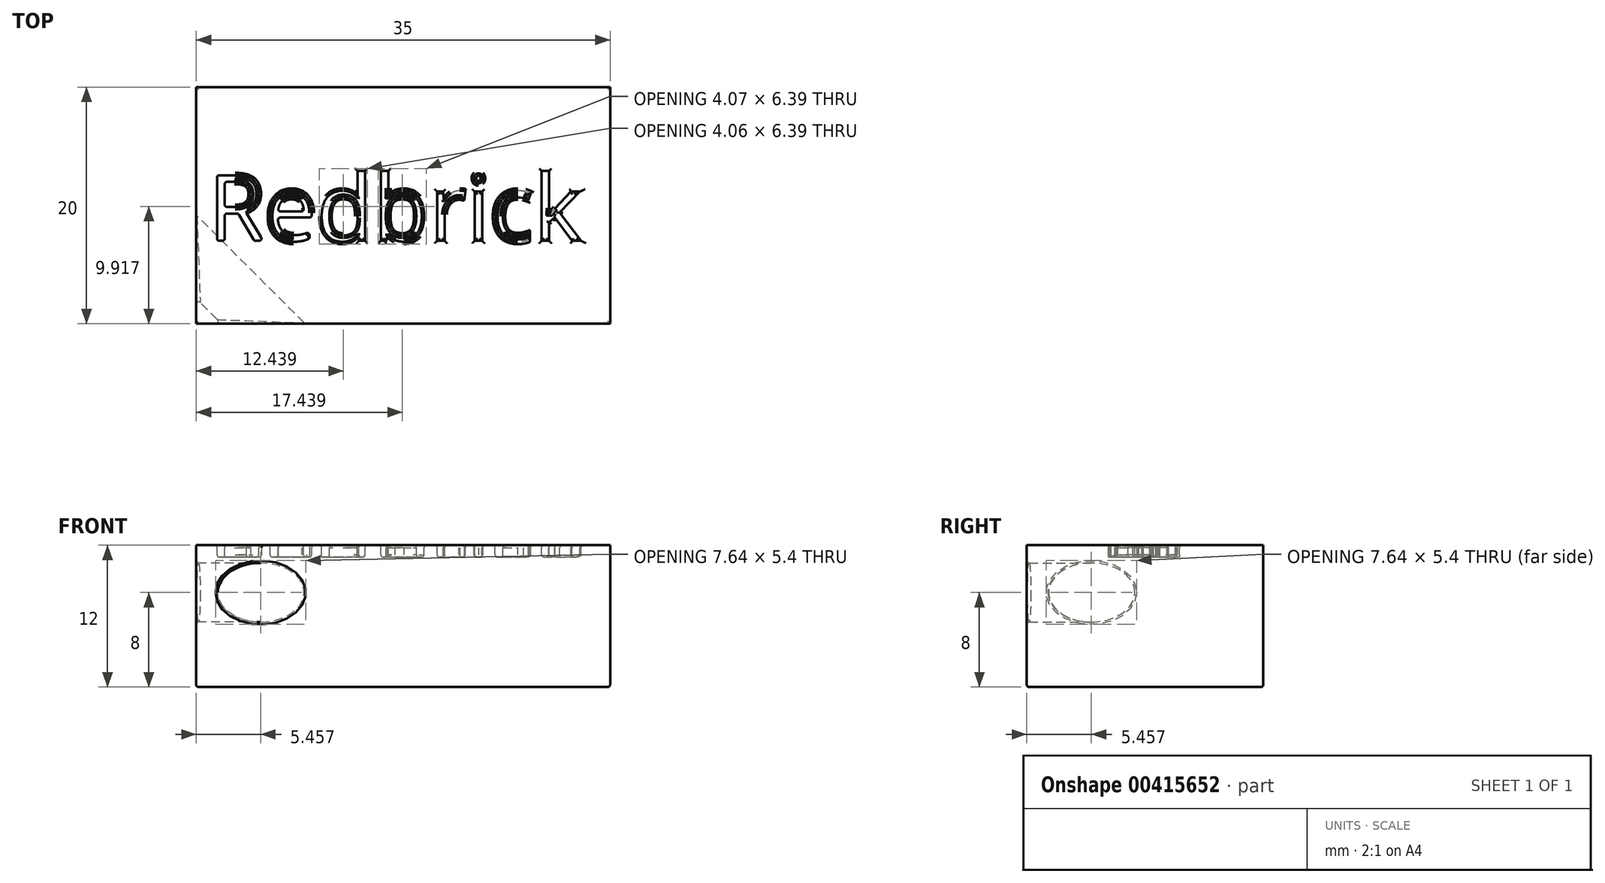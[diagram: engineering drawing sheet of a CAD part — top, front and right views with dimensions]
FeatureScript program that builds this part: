
annotation { "Feature Type Name" : "Feature", "Feature Type Description" : "" }
export const myFeature = defineFeature(function(context is Context, id is Id, definition is map)
    precondition{}
    {
        {
            var Q0;
            Q0=qCreatedBy(makeId("Top.planeOp"),FACE);
            var sketch = newSketch(context, id + "F0", { "sketchPlane" : qUnion([Q0])});
            skLineSegment(sketch, "E0.bottom", {"start": v(0, 0) * mm, "end": v(35, 0) * mm});
            skLineSegment(sketch, "E0.top", {"start": v(0, 20) * mm, "end": v(35, 20) * mm});
            skLineSegment(sketch, "E0.left", {"start": v(0, 0) * mm, "end": v(0, 20) * mm});
            skLineSegment(sketch, "E0.right", {"start": v(35, 0) * mm, "end": v(35, 20) * mm});
            skSolve(sketch);
        }
        {
            var Q0;
            Q0 = qSketchRegion(id + "F0", true);
            extrude(context, id + "F1", {"entities" : qUnion([Q0]), "depth" : 12 * mm});
        }
        {
            var Q0;
            Q0=makeQuery(id+"F1.opExtrude","SWEPT_EDGE",EDGE,{"disambiguationData":[OSD([sQuery(id+"F0.wireOp",EDGE,"E0.bottom"),sQuery(id+"F0.wireOp",EDGE,"E0.left")])]});
            cPlane(context, id + "F2", {"entities" : qUnion([Q0]), "cplaneType" : CPlaneType.LINE_ANGLE, "offset" : 25 * mm, "angle" : 45 * degree, "width" : 150 * mm, "height" : 150 * mm});
        }
        {
            var Q0;
            Q0=qCreatedBy(id+"F2.planeOp",FACE);
            var sketch = newSketch(context, id + "F3", { "sketchPlane" : qUnion([Q0])});
            skCircle(sketch, "E1", {"center": v(-4, 8) * mm, "radius": 2.5 * mm});
            skSolve(sketch);
        }
        {
            var Q0;
            Q0 = qSketchRegion(id + "F3", true);
            extrude(context, id + "F4", {"entities" : qUnion([Q0]), "operationType" : NewBodyOperationType.REMOVE, "endBound" : BoundingType.THROUGH_ALL, "oppositeDirection" : true, "depth" : 25 * mm, "hasSecondDirection" : true, "secondDirectionOppositeDirection" : false, "secondDirectionDepth" : 24.5 * mm});
        }
        {
            var Q0;
            Q0=makeQuery(id+"F1.opExtrude","CAP_FACE",FACE,{"disambiguationData":[OSD([sQuery(id+"F0.wireOp",EDGE,"E0.bottom"),sQuery(id+"F0.wireOp",EDGE,"E0.top"),sQuery(id+"F0.wireOp",EDGE,"E0.left"),sQuery(id+"F0.wireOp",EDGE,"E0.right")])],"isStart":false});
            var sketch = newSketch(context, id + "F5", { "sketchPlane" : qUnion([Q0])});
            skText(sketch, "E2", { "text": "Redbrick", "fontName": "OpenSans-Regular.ttf"});
            const initialGuessF5  = {"E2": [0.001, 0.007, 1, 0, 0.0056]};
            skSetInitialGuess(sketch, initialGuessF5);
            skSolve(sketch);
        }
        {
            var Q0;
            Q0 = qSketchRegion(id + "F5", true);
            extrude(context, id + "F6", {"entities" : qUnion([Q0]), "operationType" : NewBodyOperationType.REMOVE, "oppositeDirection" : true, "depth" : 1 * mm});
        }
        {
            var Q0;
            Q0=makeQuery(id+"F6.boolean.opBoolean","COPY",FACE,{"derivedFrom":makeQuery(id+"F6.opExtrude","SWEPT_FACE",FACE,{"disambiguationData":[OSD([sQuery(id+"F5.wireOp",EDGE,"E2.sketch_text.stroke-13")])]})});
            var Q1;
            Q1=makeQuery(id+"F6.boolean.opBoolean","COPY",FACE,{"derivedFrom":makeQuery(id+"F6.opExtrude","SWEPT_FACE",FACE,{"disambiguationData":[OSD([sQuery(id+"F5.wireOp",EDGE,"E2.sketch_text.stroke-14")])]})});
            var Q2;
            Q2=makeQuery(id+"F6.boolean.opBoolean","COPY",FACE,{"derivedFrom":makeQuery(id+"F6.opExtrude","SWEPT_FACE",FACE,{"disambiguationData":[OSD([sQuery(id+"F5.wireOp",EDGE,"E2.sketch_text.stroke-12")])]})});
            var Q3;
            Q3=makeQuery(id+"F6.boolean.opBoolean","COPY",FACE,{"derivedFrom":makeQuery(id+"F6.opExtrude","SWEPT_FACE",FACE,{"disambiguationData":[OSD([sQuery(id+"F5.wireOp",EDGE,"E2.sketch_text.stroke-0")])]})});
            var Q4;
            Q4=makeQuery(id+"F6.boolean.opBoolean","COPY",FACE,{"derivedFrom":makeQuery(id+"F6.opExtrude","CAP_FACE",FACE,{"disambiguationData":[OSD([sQuery(id+"F5.wireOp",EDGE,"E2.sketch_text.stroke-0"),sQuery(id+"F5.wireOp",EDGE,"E2.sketch_text.stroke-1"),sQuery(id+"F5.wireOp",EDGE,"E2.sketch_text.stroke-2"),sQuery(id+"F5.wireOp",EDGE,"E2.sketch_text.stroke-3"),sQuery(id+"F5.wireOp",EDGE,"E2.sketch_text.stroke-4"),sQuery(id+"F5.wireOp",EDGE,"E2.sketch_text.stroke-5"),sQuery(id+"F5.wireOp",EDGE,"E2.sketch_text.stroke-6"),sQuery(id+"F5.wireOp",EDGE,"E2.sketch_text.stroke-7"),sQuery(id+"F5.wireOp",EDGE,"E2.sketch_text.stroke-8"),sQuery(id+"F5.wireOp",EDGE,"E2.sketch_text.stroke-9"),sQuery(id+"F5.wireOp",EDGE,"E2.sketch_text.stroke-10"),sQuery(id+"F5.wireOp",EDGE,"E2.sketch_text.stroke-11"),sQuery(id+"F5.wireOp",EDGE,"E2.sketch_text.stroke-12"),sQuery(id+"F5.wireOp",EDGE,"E2.sketch_text.stroke-13"),sQuery(id+"F5.wireOp",EDGE,"E2.sketch_text.stroke-14"),sQuery(id+"F5.wireOp",EDGE,"E2.sketch_text.stroke-15"),sQuery(id+"F5.wireOp",EDGE,"E2.sketch_text.stroke-16"),sQuery(id+"F5.wireOp",EDGE,"E2.sketch_text.stroke-17")])],"isStart":false})});
            var Q5;
            Q5=makeQuery(id+"F6.boolean.opBoolean","COPY",FACE,{"derivedFrom":makeQuery(id+"F6.opExtrude","SWEPT_FACE",FACE,{"disambiguationData":[OSD([sQuery(id+"F5.wireOp",EDGE,"E2.sketch_text.stroke-1")])]})});
            var Q6;
            Q6=makeQuery(id+"F6.boolean.opBoolean","COPY",FACE,{"derivedFrom":makeQuery(id+"F6.opExtrude","SWEPT_FACE",FACE,{"disambiguationData":[OSD([sQuery(id+"F5.wireOp",EDGE,"E2.sketch_text.stroke-2")])]})});
            var Q7;
            Q7=makeQuery(id+"F6.boolean.opBoolean","COPY",FACE,{"derivedFrom":makeQuery(id+"F6.opExtrude","SWEPT_FACE",FACE,{"disambiguationData":[OSD([sQuery(id+"F5.wireOp",EDGE,"E2.sketch_text.stroke-3")])]})});
            var Q8;
            Q8=makeQuery(id+"F6.boolean.opBoolean","COPY",FACE,{"derivedFrom":makeQuery(id+"F6.opExtrude","SWEPT_FACE",FACE,{"disambiguationData":[OSD([sQuery(id+"F5.wireOp",EDGE,"E2.sketch_text.stroke-4")])]})});
            var Q9;
            Q9=makeQuery(id+"F6.boolean.opBoolean","COPY",FACE,{"derivedFrom":makeQuery(id+"F6.opExtrude","SWEPT_FACE",FACE,{"disambiguationData":[OSD([sQuery(id+"F5.wireOp",EDGE,"E2.sketch_text.stroke-5")])]})});
            var Q10;
            Q10=makeQuery(id+"F6.boolean.opBoolean","COPY",FACE,{"derivedFrom":makeQuery(id+"F6.opExtrude","SWEPT_FACE",FACE,{"disambiguationData":[OSD([sQuery(id+"F5.wireOp",EDGE,"E2.sketch_text.stroke-6")])]})});
            var Q11;
            Q11=makeQuery(id+"F6.boolean.opBoolean","COPY",FACE,{"derivedFrom":makeQuery(id+"F6.opExtrude","SWEPT_FACE",FACE,{"disambiguationData":[OSD([sQuery(id+"F5.wireOp",EDGE,"E2.sketch_text.stroke-7")])]})});
            var Q12;
            Q12=makeQuery(id+"F6.boolean.opBoolean","COPY",FACE,{"derivedFrom":makeQuery(id+"F6.opExtrude","SWEPT_FACE",FACE,{"disambiguationData":[OSD([sQuery(id+"F5.wireOp",EDGE,"E2.sketch_text.stroke-8")])]})});
            var Q13;
            Q13=makeQuery(id+"F6.boolean.opBoolean","COPY",FACE,{"derivedFrom":makeQuery(id+"F6.opExtrude","SWEPT_FACE",FACE,{"disambiguationData":[OSD([sQuery(id+"F5.wireOp",EDGE,"E2.sketch_text.stroke-9")])]})});
            var Q14;
            Q14=makeQuery(id+"F6.boolean.opBoolean","COPY",FACE,{"derivedFrom":makeQuery(id+"F6.opExtrude","SWEPT_FACE",FACE,{"disambiguationData":[OSD([sQuery(id+"F5.wireOp",EDGE,"E2.sketch_text.stroke-10")])]})});
            var Q15;
            Q15=makeQuery(id+"F6.boolean.opBoolean","COPY",FACE,{"derivedFrom":makeQuery(id+"F6.opExtrude","SWEPT_FACE",FACE,{"disambiguationData":[OSD([sQuery(id+"F5.wireOp",EDGE,"E2.sketch_text.stroke-11")])]})});
            var Q16;
            Q16=makeQuery(id+"F6.boolean.opBoolean","COPY",EDGE,{"derivedFrom":makeQuery(id+"F6.opExtrude","CAP_EDGE",EDGE,{"disambiguationData":[OSD([sQuery(id+"F5.wireOp",EDGE,"E2.sketch_text.stroke-9")])],"isStart":true})});
            var Q17;
            Q17=makeQuery(id+"F6.boolean.opBoolean","COPY",EDGE,{"derivedFrom":makeQuery(id+"F6.opExtrude","CAP_EDGE",EDGE,{"disambiguationData":[OSD([sQuery(id+"F5.wireOp",EDGE,"E2.sketch_text.stroke-2")])],"isStart":true})});
            var Q18;
            Q18=makeQuery(id+"F6.boolean.opBoolean","COPY",FACE,{"derivedFrom":makeQuery(id+"F6.opExtrude","SWEPT_FACE",FACE,{"disambiguationData":[OSD([sQuery(id+"F5.wireOp",EDGE,"E2.sketch_text.stroke-15")])]})});
            var Q19;
            Q19=makeQuery(id+"F6.boolean.opBoolean","COPY",FACE,{"derivedFrom":makeQuery(id+"F6.opExtrude","SWEPT_FACE",FACE,{"disambiguationData":[OSD([sQuery(id+"F5.wireOp",EDGE,"E2.sketch_text.stroke-16")])]})});
            var Q20;
            Q20=makeQuery(id+"F6.boolean.opBoolean","COPY",FACE,{"derivedFrom":makeQuery(id+"F6.opExtrude","SWEPT_FACE",FACE,{"disambiguationData":[OSD([sQuery(id+"F5.wireOp",EDGE,"E2.sketch_text.stroke-17")])]})});
            var Q21;
            Q21=makeQuery(id+"F6.boolean.opBoolean","SPLIT",FACE,{"disambiguationData":[TD([makeQuery(id+"F6.opExtrude","SWEPT_FACE",FACE,{"disambiguationData":[OSD([sQuery(id+"F5.wireOp",EDGE,"E2.sketch_text.stroke-11")])]})])],"derivedFrom":makeQuery(id+"F1.opExtrude","CAP_FACE",FACE,{"disambiguationData":[OSD([sQuery(id+"F0.wireOp",EDGE,"E0.bottom"),sQuery(id+"F0.wireOp",EDGE,"E0.top"),sQuery(id+"F0.wireOp",EDGE,"E0.left"),sQuery(id+"F0.wireOp",EDGE,"E0.right")])],"isStart":false})});
            var Q22;
            Q22=makeQuery(id+"F6.boolean.opBoolean","COPY",EDGE,{"derivedFrom":makeQuery(id+"F6.opExtrude","CAP_EDGE",EDGE,{"disambiguationData":[OSD([sQuery(id+"F5.wireOp",EDGE,"E2.sketch_text.stroke-7")])],"isStart":true})});
            var Q23;
            Q23=makeQuery(id+"F6.boolean.opBoolean","COPY",EDGE,{"derivedFrom":makeQuery(id+"F6.opExtrude","SWEPT_EDGE",EDGE,{"disambiguationData":[OSD([sQuery(id+"F5.wireOp",EDGE,"E2.sketch_text.stroke-0"),sQuery(id+"F5.wireOp",EDGE,"E2.sketch_text.stroke-10")])]})});
            var Q24;
            Q24=makeQuery(id+"F6.boolean.opBoolean","COPY",EDGE,{"derivedFrom":makeQuery(id+"F6.opExtrude","SWEPT_EDGE",EDGE,{"disambiguationData":[OSD([sQuery(id+"F5.wireOp",EDGE,"E2.sketch_text.stroke-13"),sQuery(id+"F5.wireOp",EDGE,"E2.sketch_text.stroke-14")])]})});
            var Q25;
            Q25=makeQuery(id+"F6.boolean.opBoolean","COPY",EDGE,{"derivedFrom":makeQuery(id+"F6.opExtrude","SWEPT_EDGE",EDGE,{"disambiguationData":[OSD([sQuery(id+"F5.wireOp",EDGE,"E2.sketch_text.stroke-14"),sQuery(id+"F5.wireOp",EDGE,"E2.sketch_text.stroke-15")])]})});
            var Q26;
            Q26=makeQuery(id+"F6.boolean.opBoolean","COPY",EDGE,{"derivedFrom":makeQuery(id+"F6.opExtrude","SWEPT_EDGE",EDGE,{"disambiguationData":[OSD([sQuery(id+"F5.wireOp",EDGE,"E2.sketch_text.stroke-12"),sQuery(id+"F5.wireOp",EDGE,"E2.sketch_text.stroke-13")])]})});
            var Q27;
            Q27=makeQuery(id+"F6.boolean.opBoolean","COPY",EDGE,{"derivedFrom":makeQuery(id+"F6.opExtrude","SWEPT_EDGE",EDGE,{"disambiguationData":[OSD([sQuery(id+"F5.wireOp",EDGE,"E2.sketch_text.stroke-0"),sQuery(id+"F5.wireOp",EDGE,"E2.sketch_text.stroke-1")])]})});
            var Q28;
            Q28=makeQuery(id+"F6.boolean.opBoolean","COPY",EDGE,{"derivedFrom":makeQuery(id+"F6.opExtrude","SWEPT_EDGE",EDGE,{"disambiguationData":[OSD([sQuery(id+"F5.wireOp",EDGE,"E2.sketch_text.stroke-1"),sQuery(id+"F5.wireOp",EDGE,"E2.sketch_text.stroke-2")])]})});
            var Q29;
            Q29=makeQuery(id+"F6.boolean.opBoolean","COPY",EDGE,{"derivedFrom":makeQuery(id+"F6.opExtrude","SWEPT_EDGE",EDGE,{"disambiguationData":[OSD([sQuery(id+"F5.wireOp",EDGE,"E2.sketch_text.stroke-2"),sQuery(id+"F5.wireOp",EDGE,"E2.sketch_text.stroke-3")])]})});
            var Q30;
            Q30=makeQuery(id+"F6.boolean.opBoolean","COPY",EDGE,{"derivedFrom":makeQuery(id+"F6.opExtrude","SWEPT_EDGE",EDGE,{"disambiguationData":[OSD([sQuery(id+"F5.wireOp",EDGE,"E2.sketch_text.stroke-3"),sQuery(id+"F5.wireOp",EDGE,"E2.sketch_text.stroke-4")])]})});
            var Q31;
            Q31=makeQuery(id+"F6.boolean.opBoolean","COPY",EDGE,{"derivedFrom":makeQuery(id+"F6.opExtrude","SWEPT_EDGE",EDGE,{"disambiguationData":[OSD([sQuery(id+"F5.wireOp",EDGE,"E2.sketch_text.stroke-4"),sQuery(id+"F5.wireOp",EDGE,"E2.sketch_text.stroke-5")])]})});
            var Q32;
            Q32=makeQuery(id+"F6.boolean.opBoolean","COPY",EDGE,{"derivedFrom":makeQuery(id+"F6.opExtrude","SWEPT_EDGE",EDGE,{"disambiguationData":[OSD([sQuery(id+"F5.wireOp",EDGE,"E2.sketch_text.stroke-5"),sQuery(id+"F5.wireOp",EDGE,"E2.sketch_text.stroke-6")])]})});
            var Q33;
            Q33=makeQuery(id+"F6.boolean.opBoolean","COPY",EDGE,{"derivedFrom":makeQuery(id+"F6.opExtrude","SWEPT_EDGE",EDGE,{"disambiguationData":[OSD([sQuery(id+"F5.wireOp",EDGE,"E2.sketch_text.stroke-6"),sQuery(id+"F5.wireOp",EDGE,"E2.sketch_text.stroke-7")])]})});
            var Q34;
            Q34=makeQuery(id+"F6.boolean.opBoolean","COPY",EDGE,{"derivedFrom":makeQuery(id+"F6.opExtrude","SWEPT_EDGE",EDGE,{"disambiguationData":[OSD([sQuery(id+"F5.wireOp",EDGE,"E2.sketch_text.stroke-7"),sQuery(id+"F5.wireOp",EDGE,"E2.sketch_text.stroke-8")])]})});
            var Q35;
            Q35=makeQuery(id+"F6.boolean.opBoolean","COPY",EDGE,{"derivedFrom":makeQuery(id+"F6.opExtrude","SWEPT_EDGE",EDGE,{"disambiguationData":[OSD([sQuery(id+"F5.wireOp",EDGE,"E2.sketch_text.stroke-8"),sQuery(id+"F5.wireOp",EDGE,"E2.sketch_text.stroke-9")])]})});
            var Q36;
            Q36=makeQuery(id+"F6.boolean.opBoolean","COPY",EDGE,{"derivedFrom":makeQuery(id+"F6.opExtrude","SWEPT_EDGE",EDGE,{"disambiguationData":[OSD([sQuery(id+"F5.wireOp",EDGE,"E2.sketch_text.stroke-9"),sQuery(id+"F5.wireOp",EDGE,"E2.sketch_text.stroke-10")])]})});
            var Q37;
            Q37=makeQuery(id+"F6.boolean.opBoolean","COPY",EDGE,{"derivedFrom":makeQuery(id+"F6.opExtrude","SWEPT_EDGE",EDGE,{"disambiguationData":[OSD([sQuery(id+"F5.wireOp",EDGE,"E2.sketch_text.stroke-11"),sQuery(id+"F5.wireOp",EDGE,"E2.sketch_text.stroke-17")])]})});
            var Q38;
            Q38=makeQuery(id+"F6.boolean.opBoolean","COPY",EDGE,{"derivedFrom":makeQuery(id+"F6.opExtrude","SWEPT_EDGE",EDGE,{"disambiguationData":[OSD([sQuery(id+"F5.wireOp",EDGE,"E2.sketch_text.stroke-11"),sQuery(id+"F5.wireOp",EDGE,"E2.sketch_text.stroke-12")])]})});
            var Q39;
            Q39=makeQuery(id+"F6.boolean.opBoolean","COPY",EDGE,{"derivedFrom":makeQuery(id+"F6.opExtrude","CAP_EDGE",EDGE,{"disambiguationData":[OSD([sQuery(id+"F5.wireOp",EDGE,"E2.sketch_text.stroke-1")])],"isStart":true})});
            var Q40;
            Q40=makeQuery(id+"F6.boolean.opBoolean","COPY",EDGE,{"derivedFrom":makeQuery(id+"F6.opExtrude","CAP_EDGE",EDGE,{"disambiguationData":[OSD([sQuery(id+"F5.wireOp",EDGE,"E2.sketch_text.stroke-17")])],"isStart":true})});
            var Q41;
            Q41=makeQuery(id+"F6.boolean.opBoolean","COPY",EDGE,{"derivedFrom":makeQuery(id+"F6.opExtrude","CAP_EDGE",EDGE,{"disambiguationData":[OSD([sQuery(id+"F5.wireOp",EDGE,"E2.sketch_text.stroke-9")])],"isStart":false})});
            var Q42;
            Q42=makeQuery(id+"F6.boolean.opBoolean","COPY",EDGE,{"derivedFrom":makeQuery(id+"F6.opExtrude","CAP_EDGE",EDGE,{"disambiguationData":[OSD([sQuery(id+"F5.wireOp",EDGE,"E2.sketch_text.stroke-10")])],"isStart":true})});
            var Q43;
            Q43=makeQuery(id+"F6.boolean.opBoolean","COPY",EDGE,{"derivedFrom":makeQuery(id+"F6.opExtrude","SWEPT_EDGE",EDGE,{"disambiguationData":[OSD([sQuery(id+"F5.wireOp",EDGE,"E2.sketch_text.stroke-15"),sQuery(id+"F5.wireOp",EDGE,"E2.sketch_text.stroke-16")])]})});
            var Q44;
            Q44=makeQuery(id+"F6.boolean.opBoolean","COPY",EDGE,{"derivedFrom":makeQuery(id+"F6.opExtrude","CAP_EDGE",EDGE,{"disambiguationData":[OSD([sQuery(id+"F5.wireOp",EDGE,"E2.sketch_text.stroke-2")])],"isStart":false})});
            var Q45;
            Q45=makeQuery(id+"F6.boolean.opBoolean","COPY",EDGE,{"derivedFrom":makeQuery(id+"F6.opExtrude","CAP_EDGE",EDGE,{"disambiguationData":[OSD([sQuery(id+"F5.wireOp",EDGE,"E2.sketch_text.stroke-3")])],"isStart":true})});
            var Q46;
            Q46=makeQuery(id+"F6.boolean.opBoolean","COPY",EDGE,{"derivedFrom":makeQuery(id+"F6.opExtrude","CAP_EDGE",EDGE,{"disambiguationData":[OSD([sQuery(id+"F5.wireOp",EDGE,"E2.sketch_text.stroke-11")])],"isStart":true})});
            var Q47;
            Q47=makeQuery(id+"F6.boolean.opBoolean","COPY",EDGE,{"derivedFrom":makeQuery(id+"F6.opExtrude","CAP_EDGE",EDGE,{"disambiguationData":[OSD([sQuery(id+"F5.wireOp",EDGE,"E2.sketch_text.stroke-4")])],"isStart":true})});
            var Q48;
            Q48=makeQuery(id+"F6.boolean.opBoolean","COPY",EDGE,{"derivedFrom":makeQuery(id+"F6.opExtrude","CAP_EDGE",EDGE,{"disambiguationData":[OSD([sQuery(id+"F5.wireOp",EDGE,"E2.sketch_text.stroke-12")])],"isStart":true})});
            var Q49;
            Q49=makeQuery(id+"F6.boolean.opBoolean","COPY",EDGE,{"derivedFrom":makeQuery(id+"F6.opExtrude","CAP_EDGE",EDGE,{"disambiguationData":[OSD([sQuery(id+"F5.wireOp",EDGE,"E2.sketch_text.stroke-5")])],"isStart":true})});
            var Q50;
            Q50=makeQuery(id+"F6.boolean.opBoolean","COPY",EDGE,{"derivedFrom":makeQuery(id+"F6.opExtrude","CAP_EDGE",EDGE,{"disambiguationData":[OSD([sQuery(id+"F5.wireOp",EDGE,"E2.sketch_text.stroke-13")])],"isStart":true})});
            var Q51;
            Q51=makeQuery(id+"F6.boolean.opBoolean","COPY",EDGE,{"derivedFrom":makeQuery(id+"F6.opExtrude","CAP_EDGE",EDGE,{"disambiguationData":[OSD([sQuery(id+"F5.wireOp",EDGE,"E2.sketch_text.stroke-6")])],"isStart":true})});
            var Q52;
            Q52=makeQuery(id+"F6.boolean.opBoolean","COPY",EDGE,{"derivedFrom":makeQuery(id+"F6.opExtrude","CAP_EDGE",EDGE,{"disambiguationData":[OSD([sQuery(id+"F5.wireOp",EDGE,"E2.sketch_text.stroke-14")])],"isStart":true})});
            var Q53;
            Q53=makeQuery(id+"F6.boolean.opBoolean","COPY",EDGE,{"derivedFrom":makeQuery(id+"F6.opExtrude","CAP_EDGE",EDGE,{"disambiguationData":[OSD([sQuery(id+"F5.wireOp",EDGE,"E2.sketch_text.stroke-15")])],"isStart":true})});
            var Q54;
            Q54=makeQuery(id+"F6.boolean.opBoolean","COPY",EDGE,{"derivedFrom":makeQuery(id+"F6.opExtrude","CAP_EDGE",EDGE,{"disambiguationData":[OSD([sQuery(id+"F5.wireOp",EDGE,"E2.sketch_text.stroke-7")])],"isStart":false})});
            var Q55;
            Q55=makeQuery(id+"F6.boolean.opBoolean","COPY",EDGE,{"derivedFrom":makeQuery(id+"F6.opExtrude","CAP_EDGE",EDGE,{"disambiguationData":[OSD([sQuery(id+"F5.wireOp",EDGE,"E2.sketch_text.stroke-0")])],"isStart":true})});
            var Q56;
            Q56=makeQuery(id+"F6.boolean.opBoolean","COPY",EDGE,{"derivedFrom":makeQuery(id+"F6.opExtrude","CAP_EDGE",EDGE,{"disambiguationData":[OSD([sQuery(id+"F5.wireOp",EDGE,"E2.sketch_text.stroke-8")])],"isStart":true})});
            var Q57;
            Q57=makeQuery(id+"F6.boolean.opBoolean","COPY",EDGE,{"derivedFrom":makeQuery(id+"F6.opExtrude","CAP_EDGE",EDGE,{"disambiguationData":[OSD([sQuery(id+"F5.wireOp",EDGE,"E2.sketch_text.stroke-16")])],"isStart":true})});
            var Q58;
            Q58=makeQuery(id+"F6.boolean.opBoolean","COPY",EDGE,{"derivedFrom":makeQuery(id+"F6.opExtrude","CAP_EDGE",EDGE,{"disambiguationData":[OSD([sQuery(id+"F5.wireOp",EDGE,"E2.sketch_text.stroke-1")])],"isStart":false})});
            var Q59;
            Q59=makeQuery(id+"F6.boolean.opBoolean","COPY",EDGE,{"derivedFrom":makeQuery(id+"F6.opExtrude","CAP_EDGE",EDGE,{"disambiguationData":[OSD([sQuery(id+"F5.wireOp",EDGE,"E2.sketch_text.stroke-17")])],"isStart":false})});
            var Q60;
            Q60=makeQuery(id+"F6.boolean.opBoolean","COPY",EDGE,{"derivedFrom":makeQuery(id+"F6.opExtrude","CAP_EDGE",EDGE,{"disambiguationData":[OSD([sQuery(id+"F5.wireOp",EDGE,"E2.sketch_text.stroke-10")])],"isStart":false})});
            var Q61;
            Q61=makeQuery(id+"F6.boolean.opBoolean","COPY",EDGE,{"derivedFrom":makeQuery(id+"F6.opExtrude","SWEPT_EDGE",EDGE,{"disambiguationData":[OSD([sQuery(id+"F5.wireOp",EDGE,"E2.sketch_text.stroke-16"),sQuery(id+"F5.wireOp",EDGE,"E2.sketch_text.stroke-17")])]})});
            var Q62;
            Q62=makeQuery(id+"F6.boolean.opBoolean","COPY",EDGE,{"derivedFrom":makeQuery(id+"F6.opExtrude","CAP_EDGE",EDGE,{"disambiguationData":[OSD([sQuery(id+"F5.wireOp",EDGE,"E2.sketch_text.stroke-3")])],"isStart":false})});
            var Q63;
            Q63=makeQuery(id+"F6.boolean.opBoolean","COPY",EDGE,{"derivedFrom":makeQuery(id+"F6.opExtrude","CAP_EDGE",EDGE,{"disambiguationData":[OSD([sQuery(id+"F5.wireOp",EDGE,"E2.sketch_text.stroke-11")])],"isStart":false})});
            var Q64;
            Q64=makeQuery(id+"F6.boolean.opBoolean","COPY",EDGE,{"derivedFrom":makeQuery(id+"F6.opExtrude","CAP_EDGE",EDGE,{"disambiguationData":[OSD([sQuery(id+"F5.wireOp",EDGE,"E2.sketch_text.stroke-4")])],"isStart":false})});
            var Q65;
            Q65=makeQuery(id+"F6.boolean.opBoolean","COPY",EDGE,{"derivedFrom":makeQuery(id+"F6.opExtrude","CAP_EDGE",EDGE,{"disambiguationData":[OSD([sQuery(id+"F5.wireOp",EDGE,"E2.sketch_text.stroke-12")])],"isStart":false})});
            var Q66;
            Q66=makeQuery(id+"F6.boolean.opBoolean","COPY",EDGE,{"derivedFrom":makeQuery(id+"F6.opExtrude","CAP_EDGE",EDGE,{"disambiguationData":[OSD([sQuery(id+"F5.wireOp",EDGE,"E2.sketch_text.stroke-5")])],"isStart":false})});
            var Q67;
            Q67=makeQuery(id+"F6.boolean.opBoolean","COPY",EDGE,{"derivedFrom":makeQuery(id+"F6.opExtrude","CAP_EDGE",EDGE,{"disambiguationData":[OSD([sQuery(id+"F5.wireOp",EDGE,"E2.sketch_text.stroke-13")])],"isStart":false})});
            var Q68;
            Q68=makeQuery(id+"F6.boolean.opBoolean","COPY",EDGE,{"derivedFrom":makeQuery(id+"F6.opExtrude","CAP_EDGE",EDGE,{"disambiguationData":[OSD([sQuery(id+"F5.wireOp",EDGE,"E2.sketch_text.stroke-6")])],"isStart":false})});
            var Q69;
            Q69=makeQuery(id+"F6.boolean.opBoolean","COPY",EDGE,{"derivedFrom":makeQuery(id+"F6.opExtrude","CAP_EDGE",EDGE,{"disambiguationData":[OSD([sQuery(id+"F5.wireOp",EDGE,"E2.sketch_text.stroke-14")])],"isStart":false})});
            var Q70;
            Q70=makeQuery(id+"F6.boolean.opBoolean","COPY",EDGE,{"derivedFrom":makeQuery(id+"F6.opExtrude","CAP_EDGE",EDGE,{"disambiguationData":[OSD([sQuery(id+"F5.wireOp",EDGE,"E2.sketch_text.stroke-15")])],"isStart":false})});
            var Q71;
            Q71=makeQuery(id+"F6.boolean.opBoolean","COPY",EDGE,{"derivedFrom":makeQuery(id+"F6.opExtrude","CAP_EDGE",EDGE,{"disambiguationData":[OSD([sQuery(id+"F5.wireOp",EDGE,"E2.sketch_text.stroke-0")])],"isStart":false})});
            var Q72;
            Q72=makeQuery(id+"F6.boolean.opBoolean","COPY",EDGE,{"derivedFrom":makeQuery(id+"F6.opExtrude","CAP_EDGE",EDGE,{"disambiguationData":[OSD([sQuery(id+"F5.wireOp",EDGE,"E2.sketch_text.stroke-8")])],"isStart":false})});
            var Q73;
            Q73=makeQuery(id+"F6.boolean.opBoolean","COPY",EDGE,{"derivedFrom":makeQuery(id+"F6.opExtrude","CAP_EDGE",EDGE,{"disambiguationData":[OSD([sQuery(id+"F5.wireOp",EDGE,"E2.sketch_text.stroke-16")])],"isStart":false})});
            fillet(context, id + "F7", {"entities" : qUnion([Q0, Q1, Q2, Q3, Q4, Q5, Q6, Q7, Q8, Q9, Q10, Q11, Q12, Q13, Q14, Q15, Q16, Q17, Q18, Q19, Q20, Q21, Q22, Q23, Q24, Q25, Q26, Q27, Q28, Q29, Q30, Q31, Q32, Q33, Q34, Q35, Q36, Q37, Q38, Q39, Q40, Q41, Q42, Q43, Q44, Q45, Q46, Q47, Q48, Q49, Q50, Q51, Q52, Q53, Q54, Q55, Q56, Q57, Q58, Q59, Q60, Q61, Q62, Q63, Q64, Q65, Q66, Q67, Q68, Q69, Q70, Q71, Q72, Q73]), "radius" : .2 * mm, "tangentPropagation" : true, "allowEdgeOverflow" : false});
        }
        {
            var Q0;
            Q0=makeQuery(id+"F6.boolean.opBoolean","COPY",EDGE,{"derivedFrom":makeQuery(id+"F6.opExtrude","CAP_EDGE",EDGE,{"disambiguationData":[OSD([sQuery(id+"F5.wireOp",EDGE,"E2.sketch_text.stroke-33")])],"isStart":true})});
            var Q1;
            Q1=makeQuery(id+"F6.boolean.opBoolean","COPY",EDGE,{"derivedFrom":makeQuery(id+"F6.opExtrude","CAP_EDGE",EDGE,{"disambiguationData":[OSD([sQuery(id+"F5.wireOp",EDGE,"E2.sketch_text.stroke-33")])],"isStart":false})});
            var Q2;
            Q2=makeQuery(id+"F6.boolean.opBoolean","COPY",EDGE,{"derivedFrom":makeQuery(id+"F6.opExtrude","CAP_EDGE",EDGE,{"disambiguationData":[OSD([sQuery(id+"F5.wireOp",EDGE,"E2.sketch_text.stroke-26")])],"isStart":true})});
            var Q3;
            Q3=makeQuery(id+"F6.boolean.opBoolean","COPY",EDGE,{"derivedFrom":makeQuery(id+"F6.opExtrude","CAP_EDGE",EDGE,{"disambiguationData":[OSD([sQuery(id+"F5.wireOp",EDGE,"E2.sketch_text.stroke-26")])],"isStart":false})});
            var Q4;
            Q4=makeQuery(id+"F6.boolean.opBoolean","COPY",FACE,{"derivedFrom":makeQuery(id+"F6.opExtrude","SWEPT_FACE",FACE,{"disambiguationData":[OSD([sQuery(id+"F5.wireOp",EDGE,"E2.sketch_text.stroke-32")])]})});
            var Q5;
            Q5=makeQuery(id+"F6.boolean.opBoolean","COPY",EDGE,{"derivedFrom":makeQuery(id+"F6.opExtrude","CAP_EDGE",EDGE,{"disambiguationData":[OSD([sQuery(id+"F5.wireOp",EDGE,"E2.sketch_text.stroke-36")])],"isStart":true})});
            var Q6;
            Q6=makeQuery(id+"F6.boolean.opBoolean","COPY",FACE,{"derivedFrom":makeQuery(id+"F6.opExtrude","SWEPT_FACE",FACE,{"disambiguationData":[OSD([sQuery(id+"F5.wireOp",EDGE,"E2.sketch_text.stroke-33")])]})});
            var Q7;
            Q7=makeQuery(id+"F6.boolean.opBoolean","COPY",EDGE,{"derivedFrom":makeQuery(id+"F6.opExtrude","CAP_EDGE",EDGE,{"disambiguationData":[OSD([sQuery(id+"F5.wireOp",EDGE,"E2.sketch_text.stroke-21")])],"isStart":true})});
            var Q8;
            Q8=makeQuery(id+"F6.boolean.opBoolean","COPY",EDGE,{"derivedFrom":makeQuery(id+"F6.opExtrude","CAP_EDGE",EDGE,{"disambiguationData":[OSD([sQuery(id+"F5.wireOp",EDGE,"E2.sketch_text.stroke-21")])],"isStart":false})});
            var Q9;
            Q9=makeQuery(id+"F6.boolean.opBoolean","COPY",FACE,{"derivedFrom":makeQuery(id+"F6.opExtrude","SWEPT_FACE",FACE,{"disambiguationData":[OSD([sQuery(id+"F5.wireOp",EDGE,"E2.sketch_text.stroke-36")])]})});
            var Q10;
            Q10=makeQuery(id+"F6.boolean.opBoolean","COPY",FACE,{"derivedFrom":makeQuery(id+"F6.opExtrude","SWEPT_FACE",FACE,{"disambiguationData":[OSD([sQuery(id+"F5.wireOp",EDGE,"E2.sketch_text.stroke-21")])]})});
            var Q11;
            Q11=makeQuery(id+"F6.boolean.opBoolean","COPY",FACE,{"derivedFrom":makeQuery(id+"F6.opExtrude","SWEPT_FACE",FACE,{"disambiguationData":[OSD([sQuery(id+"F5.wireOp",EDGE,"E2.sketch_text.stroke-26")])]})});
            var Q12;
            Q12=makeQuery(id+"F6.boolean.opBoolean","COPY",EDGE,{"derivedFrom":makeQuery(id+"F6.opExtrude","SWEPT_EDGE",EDGE,{"disambiguationData":[OSD([sQuery(id+"F5.wireOp",EDGE,"E2.sketch_text.stroke-32"),sQuery(id+"F5.wireOp",EDGE,"E2.sketch_text.stroke-36")])]})});
            var Q13;
            Q13=makeQuery(id+"F6.boolean.opBoolean","COPY",EDGE,{"derivedFrom":makeQuery(id+"F6.opExtrude","SWEPT_EDGE",EDGE,{"disambiguationData":[OSD([sQuery(id+"F5.wireOp",EDGE,"E2.sketch_text.stroke-32"),sQuery(id+"F5.wireOp",EDGE,"E2.sketch_text.stroke-33")])]})});
            var Q14;
            Q14=makeQuery(id+"F6.boolean.opBoolean","COPY",EDGE,{"derivedFrom":makeQuery(id+"F6.opExtrude","SWEPT_EDGE",EDGE,{"disambiguationData":[OSD([sQuery(id+"F5.wireOp",EDGE,"E2.sketch_text.stroke-33"),sQuery(id+"F5.wireOp",EDGE,"E2.sketch_text.stroke-34")])]})});
            var Q15;
            Q15=makeQuery(id+"F6.boolean.opBoolean","COPY",EDGE,{"derivedFrom":makeQuery(id+"F6.opExtrude","SWEPT_EDGE",EDGE,{"disambiguationData":[OSD([sQuery(id+"F5.wireOp",EDGE,"E2.sketch_text.stroke-35"),sQuery(id+"F5.wireOp",EDGE,"E2.sketch_text.stroke-36")])]})});
            var Q16;
            Q16=makeQuery(id+"F6.boolean.opBoolean","COPY",EDGE,{"derivedFrom":makeQuery(id+"F6.opExtrude","CAP_EDGE",EDGE,{"disambiguationData":[OSD([sQuery(id+"F5.wireOp",EDGE,"E2.sketch_text.stroke-36")])],"isStart":false})});
            var Q17;
            Q17=makeQuery(id+"F6.boolean.opBoolean","COPY",EDGE,{"derivedFrom":makeQuery(id+"F6.opExtrude","SWEPT_EDGE",EDGE,{"disambiguationData":[OSD([sQuery(id+"F5.wireOp",EDGE,"E2.sketch_text.stroke-20"),sQuery(id+"F5.wireOp",EDGE,"E2.sketch_text.stroke-21")])]})});
            var Q18;
            Q18=makeQuery(id+"F6.boolean.opBoolean","COPY",EDGE,{"derivedFrom":makeQuery(id+"F6.opExtrude","SWEPT_EDGE",EDGE,{"disambiguationData":[OSD([sQuery(id+"F5.wireOp",EDGE,"E2.sketch_text.stroke-21"),sQuery(id+"F5.wireOp",EDGE,"E2.sketch_text.stroke-22")])]})});
            var Q19;
            Q19=makeQuery(id+"F6.boolean.opBoolean","COPY",EDGE,{"derivedFrom":makeQuery(id+"F6.opExtrude","SWEPT_EDGE",EDGE,{"disambiguationData":[OSD([sQuery(id+"F5.wireOp",EDGE,"E2.sketch_text.stroke-25"),sQuery(id+"F5.wireOp",EDGE,"E2.sketch_text.stroke-26")])]})});
            var Q20;
            Q20=makeQuery(id+"F6.boolean.opBoolean","COPY",EDGE,{"derivedFrom":makeQuery(id+"F6.opExtrude","SWEPT_EDGE",EDGE,{"disambiguationData":[OSD([sQuery(id+"F5.wireOp",EDGE,"E2.sketch_text.stroke-26"),sQuery(id+"F5.wireOp",EDGE,"E2.sketch_text.stroke-27")])]})});
            var Q21;
            Q21=makeQuery(id+"F6.boolean.opBoolean","COPY",EDGE,{"derivedFrom":makeQuery(id+"F6.opExtrude","CAP_EDGE",EDGE,{"disambiguationData":[OSD([sQuery(id+"F5.wireOp",EDGE,"E2.sketch_text.stroke-32")])],"isStart":true})});
            var Q22;
            Q22=makeQuery(id+"F6.boolean.opBoolean","COPY",EDGE,{"derivedFrom":makeQuery(id+"F6.opExtrude","CAP_EDGE",EDGE,{"disambiguationData":[OSD([sQuery(id+"F5.wireOp",EDGE,"E2.sketch_text.stroke-32")])],"isStart":false})});
            var Q23;
            Q23=makeQuery(id+"F6.boolean.opBoolean","COPY",FACE,{"derivedFrom":makeQuery(id+"F6.opExtrude","SWEPT_FACE",FACE,{"disambiguationData":[OSD([sQuery(id+"F5.wireOp",EDGE,"E2.sketch_text.stroke-29")])]})});
            var Q24;
            Q24=makeQuery(id+"F6.boolean.opBoolean","COPY",FACE,{"derivedFrom":makeQuery(id+"F6.opExtrude","SWEPT_FACE",FACE,{"disambiguationData":[OSD([sQuery(id+"F5.wireOp",EDGE,"E2.sketch_text.stroke-27")])]})});
            var Q25;
            Q25=makeQuery(id+"F6.boolean.opBoolean","COPY",FACE,{"derivedFrom":makeQuery(id+"F6.opExtrude","SWEPT_FACE",FACE,{"disambiguationData":[OSD([sQuery(id+"F5.wireOp",EDGE,"E2.sketch_text.stroke-28")])]})});
            var Q26;
            Q26=makeQuery(id+"F6.boolean.opBoolean","COPY",EDGE,{"derivedFrom":makeQuery(id+"F6.opExtrude","CAP_EDGE",EDGE,{"disambiguationData":[OSD([sQuery(id+"F5.wireOp",EDGE,"E2.sketch_text.stroke-18")])],"isStart":true})});
            var Q27;
            Q27=makeQuery(id+"F6.boolean.opBoolean","COPY",EDGE,{"derivedFrom":makeQuery(id+"F6.opExtrude","CAP_EDGE",EDGE,{"disambiguationData":[OSD([sQuery(id+"F5.wireOp",EDGE,"E2.sketch_text.stroke-18")])],"isStart":false})});
            var Q28;
            Q28=makeQuery(id+"F6.boolean.opBoolean","COPY",FACE,{"derivedFrom":makeQuery(id+"F6.opExtrude","SWEPT_FACE",FACE,{"disambiguationData":[OSD([sQuery(id+"F5.wireOp",EDGE,"E2.sketch_text.stroke-30")])]})});
            var Q29;
            Q29=makeQuery(id+"F6.boolean.opBoolean","COPY",EDGE,{"derivedFrom":makeQuery(id+"F6.opExtrude","CAP_EDGE",EDGE,{"disambiguationData":[OSD([sQuery(id+"F5.wireOp",EDGE,"E2.sketch_text.stroke-19")])],"isStart":true})});
            var Q30;
            Q30=makeQuery(id+"F6.boolean.opBoolean","COPY",EDGE,{"derivedFrom":makeQuery(id+"F6.opExtrude","CAP_EDGE",EDGE,{"disambiguationData":[OSD([sQuery(id+"F5.wireOp",EDGE,"E2.sketch_text.stroke-27")])],"isStart":true})});
            var Q31;
            Q31=makeQuery(id+"F6.boolean.opBoolean","COPY",EDGE,{"derivedFrom":makeQuery(id+"F6.opExtrude","CAP_EDGE",EDGE,{"disambiguationData":[OSD([sQuery(id+"F5.wireOp",EDGE,"E2.sketch_text.stroke-35")])],"isStart":true})});
            var Q32;
            Q32=makeQuery(id+"F6.boolean.opBoolean","COPY",FACE,{"derivedFrom":makeQuery(id+"F6.opExtrude","SWEPT_FACE",FACE,{"disambiguationData":[OSD([sQuery(id+"F5.wireOp",EDGE,"E2.sketch_text.stroke-31")])]})});
            var Q33;
            Q33=makeQuery(id+"F6.boolean.opBoolean","COPY",EDGE,{"derivedFrom":makeQuery(id+"F6.opExtrude","CAP_EDGE",EDGE,{"disambiguationData":[OSD([sQuery(id+"F5.wireOp",EDGE,"E2.sketch_text.stroke-19")])],"isStart":false})});
            var Q34;
            Q34=makeQuery(id+"F6.boolean.opBoolean","COPY",EDGE,{"derivedFrom":makeQuery(id+"F6.opExtrude","CAP_EDGE",EDGE,{"disambiguationData":[OSD([sQuery(id+"F5.wireOp",EDGE,"E2.sketch_text.stroke-27")])],"isStart":false})});
            var Q35;
            Q35=makeQuery(id+"F6.boolean.opBoolean","COPY",EDGE,{"derivedFrom":makeQuery(id+"F6.opExtrude","CAP_EDGE",EDGE,{"disambiguationData":[OSD([sQuery(id+"F5.wireOp",EDGE,"E2.sketch_text.stroke-20")])],"isStart":true})});
            var Q36;
            Q36=makeQuery(id+"F6.boolean.opBoolean","COPY",EDGE,{"derivedFrom":makeQuery(id+"F6.opExtrude","CAP_EDGE",EDGE,{"disambiguationData":[OSD([sQuery(id+"F5.wireOp",EDGE,"E2.sketch_text.stroke-28")])],"isStart":true})});
            var Q37;
            Q37=makeQuery(id+"F6.boolean.opBoolean","COPY",FACE,{"derivedFrom":makeQuery(id+"F6.opExtrude","SWEPT_FACE",FACE,{"disambiguationData":[OSD([sQuery(id+"F5.wireOp",EDGE,"E2.sketch_text.stroke-18")])]})});
            var Q38;
            Q38=makeQuery(id+"F6.boolean.opBoolean","COPY",FACE,{"derivedFrom":makeQuery(id+"F6.opExtrude","CAP_FACE",FACE,{"disambiguationData":[OSD([sQuery(id+"F5.wireOp",EDGE,"E2.sketch_text.stroke-18"),sQuery(id+"F5.wireOp",EDGE,"E2.sketch_text.stroke-19"),sQuery(id+"F5.wireOp",EDGE,"E2.sketch_text.stroke-20"),sQuery(id+"F5.wireOp",EDGE,"E2.sketch_text.stroke-21"),sQuery(id+"F5.wireOp",EDGE,"E2.sketch_text.stroke-22"),sQuery(id+"F5.wireOp",EDGE,"E2.sketch_text.stroke-23"),sQuery(id+"F5.wireOp",EDGE,"E2.sketch_text.stroke-24"),sQuery(id+"F5.wireOp",EDGE,"E2.sketch_text.stroke-25"),sQuery(id+"F5.wireOp",EDGE,"E2.sketch_text.stroke-26"),sQuery(id+"F5.wireOp",EDGE,"E2.sketch_text.stroke-27"),sQuery(id+"F5.wireOp",EDGE,"E2.sketch_text.stroke-28"),sQuery(id+"F5.wireOp",EDGE,"E2.sketch_text.stroke-29"),sQuery(id+"F5.wireOp",EDGE,"E2.sketch_text.stroke-30"),sQuery(id+"F5.wireOp",EDGE,"E2.sketch_text.stroke-31"),sQuery(id+"F5.wireOp",EDGE,"E2.sketch_text.stroke-32"),sQuery(id+"F5.wireOp",EDGE,"E2.sketch_text.stroke-33"),sQuery(id+"F5.wireOp",EDGE,"E2.sketch_text.stroke-34"),sQuery(id+"F5.wireOp",EDGE,"E2.sketch_text.stroke-35"),sQuery(id+"F5.wireOp",EDGE,"E2.sketch_text.stroke-36")])],"isStart":false})});
            var Q39;
            Q39=makeQuery(id+"F6.boolean.opBoolean","COPY",FACE,{"derivedFrom":makeQuery(id+"F6.opExtrude","SWEPT_FACE",FACE,{"disambiguationData":[OSD([sQuery(id+"F5.wireOp",EDGE,"E2.sketch_text.stroke-34")])]})});
            var Q40;
            Q40=makeQuery(id+"F6.boolean.opBoolean","COPY",FACE,{"derivedFrom":makeQuery(id+"F6.opExtrude","SWEPT_FACE",FACE,{"disambiguationData":[OSD([sQuery(id+"F5.wireOp",EDGE,"E2.sketch_text.stroke-19")])]})});
            var Q41;
            Q41=makeQuery(id+"F6.boolean.opBoolean","COPY",FACE,{"derivedFrom":makeQuery(id+"F6.opExtrude","SWEPT_FACE",FACE,{"disambiguationData":[OSD([sQuery(id+"F5.wireOp",EDGE,"E2.sketch_text.stroke-35")])]})});
            var Q42;
            Q42=makeQuery(id+"F6.boolean.opBoolean","COPY",FACE,{"derivedFrom":makeQuery(id+"F6.opExtrude","SWEPT_FACE",FACE,{"disambiguationData":[OSD([sQuery(id+"F5.wireOp",EDGE,"E2.sketch_text.stroke-20")])]})});
            var Q43;
            Q43=makeQuery(id+"F6.boolean.opBoolean","COPY",EDGE,{"derivedFrom":makeQuery(id+"F6.opExtrude","CAP_EDGE",EDGE,{"disambiguationData":[OSD([sQuery(id+"F5.wireOp",EDGE,"E2.sketch_text.stroke-22")])],"isStart":true})});
            var Q44;
            Q44=makeQuery(id+"F6.boolean.opBoolean","COPY",EDGE,{"derivedFrom":makeQuery(id+"F6.opExtrude","CAP_EDGE",EDGE,{"disambiguationData":[OSD([sQuery(id+"F5.wireOp",EDGE,"E2.sketch_text.stroke-30")])],"isStart":true})});
            var Q45;
            Q45=makeQuery(id+"F6.boolean.opBoolean","COPY",EDGE,{"derivedFrom":makeQuery(id+"F6.opExtrude","CAP_EDGE",EDGE,{"disambiguationData":[OSD([sQuery(id+"F5.wireOp",EDGE,"E2.sketch_text.stroke-22")])],"isStart":false})});
            var Q46;
            Q46=makeQuery(id+"F6.boolean.opBoolean","COPY",FACE,{"derivedFrom":makeQuery(id+"F6.opExtrude","SWEPT_FACE",FACE,{"disambiguationData":[OSD([sQuery(id+"F5.wireOp",EDGE,"E2.sketch_text.stroke-22")])]})});
            var Q47;
            Q47=makeQuery(id+"F6.boolean.opBoolean","COPY",EDGE,{"derivedFrom":makeQuery(id+"F6.opExtrude","SWEPT_EDGE",EDGE,{"disambiguationData":[OSD([sQuery(id+"F5.wireOp",EDGE,"E2.sketch_text.stroke-40"),sQuery(id+"F5.wireOp",EDGE,"E2.sketch_text.stroke-41")])]})});
            var Q48;
            Q48=makeQuery(id+"F6.boolean.opBoolean","COPY",EDGE,{"derivedFrom":makeQuery(id+"F6.opExtrude","CAP_EDGE",EDGE,{"disambiguationData":[OSD([sQuery(id+"F5.wireOp",EDGE,"E2.sketch_text.stroke-23")])],"isStart":true})});
            var Q49;
            Q49=makeQuery(id+"F6.boolean.opBoolean","COPY",EDGE,{"derivedFrom":makeQuery(id+"F6.opExtrude","CAP_EDGE",EDGE,{"disambiguationData":[OSD([sQuery(id+"F5.wireOp",EDGE,"E2.sketch_text.stroke-31")])],"isStart":true})});
            var Q50;
            Q50=makeQuery(id+"F6.boolean.opBoolean","COPY",FACE,{"derivedFrom":makeQuery(id+"F6.opExtrude","SWEPT_FACE",FACE,{"disambiguationData":[OSD([sQuery(id+"F5.wireOp",EDGE,"E2.sketch_text.stroke-23")])]})});
            var Q51;
            Q51=makeQuery(id+"F6.boolean.opBoolean","COPY",EDGE,{"derivedFrom":makeQuery(id+"F6.opExtrude","CAP_EDGE",EDGE,{"disambiguationData":[OSD([sQuery(id+"F5.wireOp",EDGE,"E2.sketch_text.stroke-23")])],"isStart":false})});
            var Q52;
            Q52=makeQuery(id+"F6.boolean.opBoolean","COPY",FACE,{"derivedFrom":makeQuery(id+"F6.opExtrude","SWEPT_FACE",FACE,{"disambiguationData":[OSD([sQuery(id+"F5.wireOp",EDGE,"E2.sketch_text.stroke-24")])]})});
            var Q53;
            Q53=makeQuery(id+"F6.boolean.opBoolean","COPY",FACE,{"derivedFrom":makeQuery(id+"F6.opExtrude","SWEPT_FACE",FACE,{"disambiguationData":[OSD([sQuery(id+"F5.wireOp",EDGE,"E2.sketch_text.stroke-25")])]})});
            var Q54;
            {var subQ0=sQuery(id+"F5.wireOp",EDGE,"E2.sketch_text.stroke-7");Q54=makeQuery(id+"F7.opFillet","BLEND_EDGE",EDGE,{"blendedFrom":[makeQuery(id+"F6.boolean.opBoolean","COPY",VERTEX,{"derivedFrom":makeQuery(id+"F6.opExtrude","CAP_VERTEX",VERTEX,{"disambiguationData":[OSD([subQ0,sQuery(id+"F5.wireOp",EDGE,"E2.sketch_text.stroke-8")])],"isStart":true})}),makeQuery(id+"F6.boolean.opBoolean","COPY",EDGE,{"derivedFrom":makeQuery(id+"F6.opExtrude","CAP_EDGE",EDGE,{"disambiguationData":[OSD([subQ0])],"isStart":true})})],"blendedInto":[]});}
            var Q55;
            Q55=makeQuery(id+"F6.boolean.opBoolean","COPY",EDGE,{"derivedFrom":makeQuery(id+"F6.opExtrude","SWEPT_EDGE",EDGE,{"disambiguationData":[OSD([sQuery(id+"F5.wireOp",EDGE,"E2.sketch_text.stroke-28"),sQuery(id+"F5.wireOp",EDGE,"E2.sketch_text.stroke-29")])]})});
            var Q56;
            Q56=makeQuery(id+"F6.boolean.opBoolean","COPY",EDGE,{"derivedFrom":makeQuery(id+"F6.opExtrude","CAP_EDGE",EDGE,{"disambiguationData":[OSD([sQuery(id+"F5.wireOp",EDGE,"E2.sketch_text.stroke-25")])],"isStart":true})});
            var Q57;
            Q57=makeQuery(id+"F6.boolean.opBoolean","COPY",EDGE,{"derivedFrom":makeQuery(id+"F6.opExtrude","SWEPT_EDGE",EDGE,{"disambiguationData":[OSD([sQuery(id+"F5.wireOp",EDGE,"E2.sketch_text.stroke-29"),sQuery(id+"F5.wireOp",EDGE,"E2.sketch_text.stroke-30")])]})});
            var Q58;
            Q58=makeQuery(id+"F6.boolean.opBoolean","COPY",EDGE,{"derivedFrom":makeQuery(id+"F6.opExtrude","CAP_EDGE",EDGE,{"disambiguationData":[OSD([sQuery(id+"F5.wireOp",EDGE,"E2.sketch_text.stroke-25")])],"isStart":false})});
            var Q59;
            Q59=makeQuery(id+"F6.boolean.opBoolean","COPY",EDGE,{"derivedFrom":makeQuery(id+"F6.opExtrude","SWEPT_EDGE",EDGE,{"disambiguationData":[OSD([sQuery(id+"F5.wireOp",EDGE,"E2.sketch_text.stroke-30"),sQuery(id+"F5.wireOp",EDGE,"E2.sketch_text.stroke-31")])]})});
            var Q60;
            Q60=makeQuery(id+"F6.boolean.opBoolean","COPY",EDGE,{"derivedFrom":makeQuery(id+"F6.opExtrude","CAP_EDGE",EDGE,{"disambiguationData":[OSD([sQuery(id+"F5.wireOp",EDGE,"E2.sketch_text.stroke-34")])],"isStart":true})});
            var Q61;
            Q61=makeQuery(id+"F6.boolean.opBoolean","COPY",EDGE,{"derivedFrom":makeQuery(id+"F6.opExtrude","SWEPT_EDGE",EDGE,{"disambiguationData":[OSD([sQuery(id+"F5.wireOp",EDGE,"E2.sketch_text.stroke-18"),sQuery(id+"F5.wireOp",EDGE,"E2.sketch_text.stroke-31")])]})});
            var Q62;
            Q62=makeQuery(id+"F6.boolean.opBoolean","COPY",EDGE,{"derivedFrom":makeQuery(id+"F6.opExtrude","CAP_EDGE",EDGE,{"disambiguationData":[OSD([sQuery(id+"F5.wireOp",EDGE,"E2.sketch_text.stroke-35")])],"isStart":false})});
            var Q63;
            Q63=makeQuery(id+"F6.boolean.opBoolean","COPY",EDGE,{"derivedFrom":makeQuery(id+"F6.opExtrude","SWEPT_EDGE",EDGE,{"disambiguationData":[OSD([sQuery(id+"F5.wireOp",EDGE,"E2.sketch_text.stroke-18"),sQuery(id+"F5.wireOp",EDGE,"E2.sketch_text.stroke-19")])]})});
            var Q64;
            Q64=makeQuery(id+"F6.boolean.opBoolean","COPY",EDGE,{"derivedFrom":makeQuery(id+"F6.opExtrude","SWEPT_EDGE",EDGE,{"disambiguationData":[OSD([sQuery(id+"F5.wireOp",EDGE,"E2.sketch_text.stroke-19"),sQuery(id+"F5.wireOp",EDGE,"E2.sketch_text.stroke-20")])]})});
            var Q65;
            Q65=makeQuery(id+"F6.boolean.opBoolean","COPY",EDGE,{"derivedFrom":makeQuery(id+"F6.opExtrude","CAP_EDGE",EDGE,{"disambiguationData":[OSD([sQuery(id+"F5.wireOp",EDGE,"E2.sketch_text.stroke-20")])],"isStart":false})});
            var Q66;
            Q66=makeQuery(id+"F6.boolean.opBoolean","COPY",EDGE,{"derivedFrom":makeQuery(id+"F6.opExtrude","CAP_EDGE",EDGE,{"disambiguationData":[OSD([sQuery(id+"F5.wireOp",EDGE,"E2.sketch_text.stroke-28")])],"isStart":false})});
            var Q67;
            Q67=makeQuery(id+"F6.boolean.opBoolean","COPY",EDGE,{"derivedFrom":makeQuery(id+"F6.opExtrude","CAP_EDGE",EDGE,{"disambiguationData":[OSD([sQuery(id+"F5.wireOp",EDGE,"E2.sketch_text.stroke-29")])],"isStart":true})});
            var Q68;
            Q68=makeQuery(id+"F6.boolean.opBoolean","COPY",EDGE,{"derivedFrom":makeQuery(id+"F6.opExtrude","SWEPT_EDGE",EDGE,{"disambiguationData":[OSD([sQuery(id+"F5.wireOp",EDGE,"E2.sketch_text.stroke-22"),sQuery(id+"F5.wireOp",EDGE,"E2.sketch_text.stroke-23")])]})});
            var Q69;
            Q69=makeQuery(id+"F6.boolean.opBoolean","COPY",EDGE,{"derivedFrom":makeQuery(id+"F6.opExtrude","SWEPT_EDGE",EDGE,{"disambiguationData":[OSD([sQuery(id+"F5.wireOp",EDGE,"E2.sketch_text.stroke-23"),sQuery(id+"F5.wireOp",EDGE,"E2.sketch_text.stroke-24")])]})});
            var Q70;
            Q70=makeQuery(id+"F6.boolean.opBoolean","COPY",EDGE,{"derivedFrom":makeQuery(id+"F6.opExtrude","CAP_EDGE",EDGE,{"disambiguationData":[OSD([sQuery(id+"F5.wireOp",EDGE,"E2.sketch_text.stroke-30")])],"isStart":false})});
            var Q71;
            Q71=makeQuery(id+"F6.boolean.opBoolean","COPY",EDGE,{"derivedFrom":makeQuery(id+"F6.opExtrude","CAP_EDGE",EDGE,{"disambiguationData":[OSD([sQuery(id+"F5.wireOp",EDGE,"E2.sketch_text.stroke-31")])],"isStart":false})});
            var Q72;
            Q72=makeQuery(id+"F6.boolean.opBoolean","COPY",EDGE,{"derivedFrom":makeQuery(id+"F6.opExtrude","CAP_EDGE",EDGE,{"disambiguationData":[OSD([sQuery(id+"F5.wireOp",EDGE,"E2.sketch_text.stroke-24")])],"isStart":true})});
            var Q73;
            Q73=makeQuery(id+"F6.boolean.opBoolean","COPY",EDGE,{"derivedFrom":makeQuery(id+"F6.opExtrude","SWEPT_EDGE",EDGE,{"disambiguationData":[OSD([sQuery(id+"F5.wireOp",EDGE,"E2.sketch_text.stroke-27"),sQuery(id+"F5.wireOp",EDGE,"E2.sketch_text.stroke-28")])]})});
            var Q74;
            {var subQ0=sQuery(id+"F5.wireOp",EDGE,"E2.sketch_text.stroke-7");Q74=makeQuery(id+"F7.opFillet","BLEND_EDGE",EDGE,{"blendedFrom":[makeQuery(id+"F6.boolean.opBoolean","COPY",EDGE,{"derivedFrom":makeQuery(id+"F6.opExtrude","SWEPT_EDGE",EDGE,{"disambiguationData":[OSD([subQ0,sQuery(id+"F5.wireOp",EDGE,"E2.sketch_text.stroke-8")])]})}),makeQuery(id+"F6.boolean.opBoolean","COPY",FACE,{"derivedFrom":makeQuery(id+"F6.opExtrude","SWEPT_FACE",FACE,{"disambiguationData":[OSD([subQ0])]})})],"blendedInto":[makeQuery(id+"F6.boolean.opBoolean","COPY",FACE,{"derivedFrom":makeQuery(id+"F6.opExtrude","SWEPT_FACE",FACE,{"disambiguationData":[OSD([subQ0])]})})]});}
            var Q75;
            Q75=makeQuery(id+"F6.boolean.opBoolean","COPY",EDGE,{"derivedFrom":makeQuery(id+"F6.opExtrude","CAP_EDGE",EDGE,{"disambiguationData":[OSD([sQuery(id+"F5.wireOp",EDGE,"E2.sketch_text.stroke-34")])],"isStart":false})});
            var Q76;
            Q76=makeQuery(id+"F6.boolean.opBoolean","COPY",EDGE,{"derivedFrom":makeQuery(id+"F6.opExtrude","SWEPT_EDGE",EDGE,{"disambiguationData":[OSD([sQuery(id+"F5.wireOp",EDGE,"E2.sketch_text.stroke-34"),sQuery(id+"F5.wireOp",EDGE,"E2.sketch_text.stroke-35")])]})});
            var Q77;
            Q77=makeQuery(id+"F6.boolean.opBoolean","COPY",EDGE,{"derivedFrom":makeQuery(id+"F6.opExtrude","CAP_EDGE",EDGE,{"disambiguationData":[OSD([sQuery(id+"F5.wireOp",EDGE,"E2.sketch_text.stroke-29")])],"isStart":false})});
            var Q78;
            Q78=makeQuery(id+"F6.boolean.opBoolean","COPY",EDGE,{"derivedFrom":makeQuery(id+"F6.opExtrude","SWEPT_EDGE",EDGE,{"disambiguationData":[OSD([sQuery(id+"F5.wireOp",EDGE,"E2.sketch_text.stroke-24"),sQuery(id+"F5.wireOp",EDGE,"E2.sketch_text.stroke-25")])]})});
            var Q79;
            Q79=makeQuery(id+"F6.boolean.opBoolean","COPY",EDGE,{"derivedFrom":makeQuery(id+"F6.opExtrude","CAP_EDGE",EDGE,{"disambiguationData":[OSD([sQuery(id+"F5.wireOp",EDGE,"E2.sketch_text.stroke-24")])],"isStart":false})});
            fillet(context, id + "F8", {"entities" : qUnion([Q0, Q1, Q2, Q3, Q4, Q5, Q6, Q7, Q8, Q9, Q10, Q11, Q12, Q13, Q14, Q15, Q16, Q17, Q18, Q19, Q20, Q21, Q22, Q23, Q24, Q25, Q26, Q27, Q28, Q29, Q30, Q31, Q32, Q33, Q34, Q35, Q36, Q37, Q38, Q39, Q40, Q41, Q42, Q43, Q44, Q45, Q46, Q47, Q48, Q49, Q50, Q51, Q52, Q53, Q54, Q55, Q56, Q57, Q58, Q59, Q60, Q61, Q62, Q63, Q64, Q65, Q66, Q67, Q68, Q69, Q70, Q71, Q72, Q73, Q74, Q75, Q76, Q77, Q78, Q79]), "radius" : .2 * mm, "tangentPropagation" : true, "allowEdgeOverflow" : false});
        }
        {
            var Q0;
            Q0=makeQuery(id+"F6.boolean.opBoolean","COPY",EDGE,{"derivedFrom":makeQuery(id+"F6.opExtrude","CAP_EDGE",EDGE,{"disambiguationData":[OSD([sQuery(id+"F5.wireOp",EDGE,"E2.sketch_text.stroke-43")])],"isStart":true})});
            var Q1;
            Q1=makeQuery(id+"F6.boolean.opBoolean","COPY",EDGE,{"derivedFrom":makeQuery(id+"F6.opExtrude","CAP_EDGE",EDGE,{"disambiguationData":[OSD([sQuery(id+"F5.wireOp",EDGE,"E2.sketch_text.stroke-42")])],"isStart":true})});
            var Q2;
            Q2=makeQuery(id+"F6.boolean.opBoolean","COPY",EDGE,{"derivedFrom":makeQuery(id+"F6.opExtrude","CAP_EDGE",EDGE,{"disambiguationData":[OSD([sQuery(id+"F5.wireOp",EDGE,"E2.sketch_text.stroke-55")])],"isStart":true})});
            var Q3;
            Q3=makeQuery(id+"F6.boolean.opBoolean","COPY",EDGE,{"derivedFrom":makeQuery(id+"F6.opExtrude","CAP_EDGE",EDGE,{"disambiguationData":[OSD([sQuery(id+"F5.wireOp",EDGE,"E2.sketch_text.stroke-47")])],"isStart":true})});
            var Q4;
            Q4=makeQuery(id+"F6.boolean.opBoolean","COPY",EDGE,{"derivedFrom":makeQuery(id+"F6.opExtrude","CAP_EDGE",EDGE,{"disambiguationData":[OSD([sQuery(id+"F5.wireOp",EDGE,"E2.sketch_text.stroke-49")])],"isStart":true})});
            var Q5;
            Q5=makeQuery(id+"F6.boolean.opBoolean","COPY",EDGE,{"derivedFrom":makeQuery(id+"F6.opExtrude","CAP_EDGE",EDGE,{"disambiguationData":[OSD([sQuery(id+"F5.wireOp",EDGE,"E2.sketch_text.stroke-51")])],"isStart":true})});
            var Q6;
            Q6=makeQuery(id+"F6.boolean.opBoolean","COPY",EDGE,{"derivedFrom":makeQuery(id+"F6.opExtrude","CAP_EDGE",EDGE,{"disambiguationData":[OSD([sQuery(id+"F5.wireOp",EDGE,"E2.sketch_text.stroke-50")])],"isStart":true})});
            var Q7;
            Q7=makeQuery(id+"F6.boolean.opBoolean","COPY",EDGE,{"derivedFrom":makeQuery(id+"F6.opExtrude","CAP_EDGE",EDGE,{"disambiguationData":[OSD([sQuery(id+"F5.wireOp",EDGE,"E2.sketch_text.stroke-48")])],"isStart":true})});
            var Q8;
            Q8=makeQuery(id+"F6.boolean.opBoolean","COPY",EDGE,{"derivedFrom":makeQuery(id+"F6.opExtrude","CAP_EDGE",EDGE,{"disambiguationData":[OSD([sQuery(id+"F5.wireOp",EDGE,"E2.sketch_text.stroke-47")])],"isStart":false})});
            var Q9;
            Q9=makeQuery(id+"F6.boolean.opBoolean","COPY",EDGE,{"derivedFrom":makeQuery(id+"F6.opExtrude","CAP_EDGE",EDGE,{"disambiguationData":[OSD([sQuery(id+"F5.wireOp",EDGE,"E2.sketch_text.stroke-49")])],"isStart":false})});
            var Q10;
            Q10=makeQuery(id+"F6.boolean.opBoolean","COPY",EDGE,{"derivedFrom":makeQuery(id+"F6.opExtrude","CAP_EDGE",EDGE,{"disambiguationData":[OSD([sQuery(id+"F5.wireOp",EDGE,"E2.sketch_text.stroke-50")])],"isStart":false})});
            var Q11;
            Q11=makeQuery(id+"F6.boolean.opBoolean","COPY",EDGE,{"derivedFrom":makeQuery(id+"F6.opExtrude","CAP_EDGE",EDGE,{"disambiguationData":[OSD([sQuery(id+"F5.wireOp",EDGE,"E2.sketch_text.stroke-51")])],"isStart":false})});
            var Q12;
            Q12=makeQuery(id+"F6.boolean.opBoolean","COPY",EDGE,{"derivedFrom":makeQuery(id+"F6.opExtrude","CAP_EDGE",EDGE,{"disambiguationData":[OSD([sQuery(id+"F5.wireOp",EDGE,"E2.sketch_text.stroke-53")])],"isStart":false})});
            fillet(context, id + "F9", {"entities" : qUnion([Q0, Q1, Q2, Q3, Q4, Q5, Q6, Q7, Q8, Q9, Q10, Q11, Q12]), "radius" : .2 * mm, "tangentPropagation" : true, "allowEdgeOverflow" : false});
        }
        {
            var Q0;
            Q0=makeQuery(id+"F6.boolean.opBoolean","COPY",EDGE,{"derivedFrom":makeQuery(id+"F6.opExtrude","CAP_EDGE",EDGE,{"disambiguationData":[OSD([sQuery(id+"F5.wireOp",EDGE,"E2.sketch_text.stroke-70")])],"isStart":true})});
            var Q1;
            Q1=makeQuery(id+"F6.boolean.opBoolean","COPY",EDGE,{"derivedFrom":makeQuery(id+"F6.opExtrude","CAP_EDGE",EDGE,{"disambiguationData":[OSD([sQuery(id+"F5.wireOp",EDGE,"E2.sketch_text.stroke-70")])],"isStart":false})});
            var Q2;
            Q2=makeQuery(id+"F6.boolean.opBoolean","COPY",EDGE,{"derivedFrom":makeQuery(id+"F6.opExtrude","CAP_EDGE",EDGE,{"disambiguationData":[OSD([sQuery(id+"F5.wireOp",EDGE,"E2.sketch_text.stroke-71")])],"isStart":true})});
            var Q3;
            Q3=makeQuery(id+"F6.boolean.opBoolean","COPY",EDGE,{"derivedFrom":makeQuery(id+"F6.opExtrude","CAP_EDGE",EDGE,{"disambiguationData":[OSD([sQuery(id+"F5.wireOp",EDGE,"E2.sketch_text.stroke-72")])],"isStart":true})});
            var Q4;
            Q4=makeQuery(id+"F6.boolean.opBoolean","COPY",EDGE,{"derivedFrom":makeQuery(id+"F6.opExtrude","CAP_EDGE",EDGE,{"disambiguationData":[OSD([sQuery(id+"F5.wireOp",EDGE,"E2.sketch_text.stroke-75")])],"isStart":true})});
            var Q5;
            Q5=makeQuery(id+"F6.boolean.opBoolean","COPY",EDGE,{"derivedFrom":makeQuery(id+"F6.opExtrude","CAP_EDGE",EDGE,{"disambiguationData":[OSD([sQuery(id+"F5.wireOp",EDGE,"E2.sketch_text.stroke-75")])],"isStart":false})});
            var Q6;
            Q6=makeQuery(id+"F6.boolean.opBoolean","COPY",EDGE,{"derivedFrom":makeQuery(id+"F6.opExtrude","CAP_EDGE",EDGE,{"disambiguationData":[OSD([sQuery(id+"F5.wireOp",EDGE,"E2.sketch_text.stroke-82")])],"isStart":true})});
            var Q7;
            Q7=makeQuery(id+"F6.boolean.opBoolean","COPY",EDGE,{"derivedFrom":makeQuery(id+"F6.opExtrude","CAP_EDGE",EDGE,{"disambiguationData":[OSD([sQuery(id+"F5.wireOp",EDGE,"E2.sketch_text.stroke-82")])],"isStart":false})});
            var Q8;
            Q8=makeQuery(id+"F6.boolean.opBoolean","COPY",EDGE,{"derivedFrom":makeQuery(id+"F6.opExtrude","CAP_EDGE",EDGE,{"disambiguationData":[OSD([sQuery(id+"F5.wireOp",EDGE,"E2.sketch_text.stroke-69")])],"isStart":true})});
            var Q9;
            Q9=makeQuery(id+"F6.boolean.opBoolean","COPY",EDGE,{"derivedFrom":makeQuery(id+"F6.opExtrude","CAP_EDGE",EDGE,{"disambiguationData":[OSD([sQuery(id+"F5.wireOp",EDGE,"E2.sketch_text.stroke-68")])],"isStart":false})});
            var Q10;
            Q10=makeQuery(id+"F6.boolean.opBoolean","COPY",EDGE,{"derivedFrom":makeQuery(id+"F6.opExtrude","CAP_EDGE",EDGE,{"disambiguationData":[OSD([sQuery(id+"F5.wireOp",EDGE,"E2.sketch_text.stroke-69")])],"isStart":false})});
            var Q11;
            Q11=makeQuery(id+"F6.boolean.opBoolean","COPY",EDGE,{"derivedFrom":makeQuery(id+"F6.opExtrude","CAP_EDGE",EDGE,{"disambiguationData":[OSD([sQuery(id+"F5.wireOp",EDGE,"E2.sketch_text.stroke-72")])],"isStart":false})});
            fillet(context, id + "F10", {"entities" : qUnion([Q0, Q1, Q2, Q3, Q4, Q5, Q6, Q7, Q8, Q9, Q10, Q11]), "radius" : .2 * mm, "tangentPropagation" : true, "allowEdgeOverflow" : false});
        }
        {
            var Q0;
            Q0=makeQuery(id+"F6.boolean.opBoolean","COPY",EDGE,{"derivedFrom":makeQuery(id+"F6.opExtrude","CAP_EDGE",EDGE,{"disambiguationData":[OSD([sQuery(id+"F5.wireOp",EDGE,"E2.sketch_text.stroke-92")])],"isStart":true})});
            var Q1;
            Q1=makeQuery(id+"F6.boolean.opBoolean","COPY",EDGE,{"derivedFrom":makeQuery(id+"F6.opExtrude","CAP_EDGE",EDGE,{"disambiguationData":[OSD([sQuery(id+"F5.wireOp",EDGE,"E2.sketch_text.stroke-91")])],"isStart":true})});
            var Q2;
            Q2=makeQuery(id+"F6.boolean.opBoolean","COPY",EDGE,{"derivedFrom":makeQuery(id+"F6.opExtrude","CAP_EDGE",EDGE,{"disambiguationData":[OSD([sQuery(id+"F5.wireOp",EDGE,"E2.sketch_text.stroke-95")])],"isStart":true})});
            var Q3;
            Q3=makeQuery(id+"F6.boolean.opBoolean","COPY",EDGE,{"derivedFrom":makeQuery(id+"F6.opExtrude","CAP_EDGE",EDGE,{"disambiguationData":[OSD([sQuery(id+"F5.wireOp",EDGE,"E2.sketch_text.stroke-93")])],"isStart":true})});
            var Q4;
            Q4=makeQuery(id+"F6.boolean.opBoolean","COPY",EDGE,{"derivedFrom":makeQuery(id+"F6.opExtrude","CAP_EDGE",EDGE,{"disambiguationData":[OSD([sQuery(id+"F5.wireOp",EDGE,"E2.sketch_text.stroke-88")])],"isStart":true})});
            var Q5;
            Q5=makeQuery(id+"F6.boolean.opBoolean","COPY",EDGE,{"derivedFrom":makeQuery(id+"F6.opExtrude","CAP_EDGE",EDGE,{"disambiguationData":[OSD([sQuery(id+"F5.wireOp",EDGE,"E2.sketch_text.stroke-90")])],"isStart":true})});
            var Q6;
            Q6=makeQuery(id+"F6.boolean.opBoolean","COPY",EDGE,{"derivedFrom":makeQuery(id+"F6.opExtrude","CAP_EDGE",EDGE,{"disambiguationData":[OSD([sQuery(id+"F5.wireOp",EDGE,"E2.sketch_text.stroke-92")])],"isStart":false})});
            var Q7;
            Q7=makeQuery(id+"F6.boolean.opBoolean","COPY",EDGE,{"derivedFrom":makeQuery(id+"F6.opExtrude","CAP_EDGE",EDGE,{"disambiguationData":[OSD([sQuery(id+"F5.wireOp",EDGE,"E2.sketch_text.stroke-93")])],"isStart":false})});
            var Q8;
            Q8=makeQuery(id+"F6.boolean.opBoolean","COPY",EDGE,{"derivedFrom":makeQuery(id+"F6.opExtrude","CAP_EDGE",EDGE,{"disambiguationData":[OSD([sQuery(id+"F5.wireOp",EDGE,"E2.sketch_text.stroke-91")])],"isStart":false})});
            var Q9;
            Q9=makeQuery(id+"F6.boolean.opBoolean","COPY",EDGE,{"derivedFrom":makeQuery(id+"F6.opExtrude","CAP_EDGE",EDGE,{"disambiguationData":[OSD([sQuery(id+"F5.wireOp",EDGE,"E2.sketch_text.stroke-88")])],"isStart":false})});
            var Q10;
            Q10=makeQuery(id+"F6.boolean.opBoolean","COPY",EDGE,{"derivedFrom":makeQuery(id+"F6.opExtrude","CAP_EDGE",EDGE,{"disambiguationData":[OSD([sQuery(id+"F5.wireOp",EDGE,"E2.sketch_text.stroke-85")])],"isStart":false})});
            var Q11;
            Q11=makeQuery(id+"F6.boolean.opBoolean","COPY",EDGE,{"derivedFrom":makeQuery(id+"F6.opExtrude","CAP_EDGE",EDGE,{"disambiguationData":[OSD([sQuery(id+"F5.wireOp",EDGE,"E2.sketch_text.stroke-90")])],"isStart":false})});
            var Q12;
            Q12=makeQuery(id+"F6.boolean.opBoolean","COPY",EDGE,{"derivedFrom":makeQuery(id+"F6.opExtrude","CAP_EDGE",EDGE,{"disambiguationData":[OSD([sQuery(id+"F5.wireOp",EDGE,"E2.sketch_text.stroke-98")])],"isStart":true})});
            var Q13;
            Q13=makeQuery(id+"F6.boolean.opBoolean","COPY",EDGE,{"derivedFrom":makeQuery(id+"F6.opExtrude","CAP_EDGE",EDGE,{"disambiguationData":[OSD([sQuery(id+"F5.wireOp",EDGE,"E2.sketch_text.stroke-100")])],"isStart":true})});
            var Q14;
            Q14=makeQuery(id+"F6.boolean.opBoolean","COPY",EDGE,{"derivedFrom":makeQuery(id+"F6.opExtrude","CAP_EDGE",EDGE,{"disambiguationData":[OSD([sQuery(id+"F5.wireOp",EDGE,"E2.sketch_text.stroke-99")])],"isStart":true})});
            var Q15;
            Q15=makeQuery(id+"F6.boolean.opBoolean","COPY",EDGE,{"derivedFrom":makeQuery(id+"F6.opExtrude","CAP_EDGE",EDGE,{"disambiguationData":[OSD([sQuery(id+"F5.wireOp",EDGE,"E2.sketch_text.stroke-106")])],"isStart":true})});
            var Q16;
            Q16=makeQuery(id+"F6.boolean.opBoolean","COPY",EDGE,{"derivedFrom":makeQuery(id+"F6.opExtrude","CAP_EDGE",EDGE,{"disambiguationData":[OSD([sQuery(id+"F5.wireOp",EDGE,"E2.sketch_text.stroke-106")])],"isStart":false})});
            var Q17;
            Q17=makeQuery(id+"F6.boolean.opBoolean","COPY",EDGE,{"derivedFrom":makeQuery(id+"F6.opExtrude","CAP_EDGE",EDGE,{"disambiguationData":[OSD([sQuery(id+"F5.wireOp",EDGE,"E2.sketch_text.stroke-97")])],"isStart":true})});
            var Q18;
            Q18=makeQuery(id+"F6.boolean.opBoolean","COPY",EDGE,{"derivedFrom":makeQuery(id+"F6.opExtrude","CAP_EDGE",EDGE,{"disambiguationData":[OSD([sQuery(id+"F5.wireOp",EDGE,"E2.sketch_text.stroke-97")])],"isStart":false})});
            var Q19;
            Q19=makeQuery(id+"F6.boolean.opBoolean","COPY",EDGE,{"derivedFrom":makeQuery(id+"F6.opExtrude","CAP_EDGE",EDGE,{"disambiguationData":[OSD([sQuery(id+"F5.wireOp",EDGE,"E2.sketch_text.stroke-98")])],"isStart":false})});
            var Q20;
            Q20=makeQuery(id+"F6.boolean.opBoolean","COPY",EDGE,{"derivedFrom":makeQuery(id+"F6.opExtrude","CAP_EDGE",EDGE,{"disambiguationData":[OSD([sQuery(id+"F5.wireOp",EDGE,"E2.sketch_text.stroke-99")])],"isStart":false})});
            var Q21;
            Q21=makeQuery(id+"F6.boolean.opBoolean","COPY",EDGE,{"derivedFrom":makeQuery(id+"F6.opExtrude","CAP_EDGE",EDGE,{"disambiguationData":[OSD([sQuery(id+"F5.wireOp",EDGE,"E2.sketch_text.stroke-100")])],"isStart":false})});
            fillet(context, id + "F11", {"entities" : qUnion([Q0, Q1, Q2, Q3, Q4, Q5, Q6, Q7, Q8, Q9, Q10, Q11, Q12, Q13, Q14, Q15, Q16, Q17, Q18, Q19, Q20, Q21]), "radius" : .2 * mm, "tangentPropagation" : true, "allowEdgeOverflow" : false});
        }
        {
            var Q0;
            Q0=makeQuery(id+"F1.opExtrude","CAP_FACE",FACE,{"disambiguationData":[OSD([sQuery(id+"F0.wireOp",EDGE,"E0.bottom"),sQuery(id+"F0.wireOp",EDGE,"E0.top"),sQuery(id+"F0.wireOp",EDGE,"E0.left"),sQuery(id+"F0.wireOp",EDGE,"E0.right")])],"isStart":true});
            var Q1;
            Q1=makeQuery(id+"F6.boolean.opBoolean","COPY",EDGE,{"derivedFrom":makeQuery(id+"F6.opExtrude","CAP_EDGE",EDGE,{"disambiguationData":[OSD([sQuery(id+"F5.wireOp",EDGE,"E2.sketch_text.stroke-112")])],"isStart":true})});
            var Q2;
            Q2=makeQuery(id+"F6.boolean.opBoolean","COPY",EDGE,{"derivedFrom":makeQuery(id+"F6.opExtrude","CAP_EDGE",EDGE,{"disambiguationData":[OSD([sQuery(id+"F5.wireOp",EDGE,"E2.sketch_text.stroke-118")])],"isStart":true})});
            var Q3;
            Q3=makeQuery(id+"F6.boolean.opBoolean","COPY",EDGE,{"derivedFrom":makeQuery(id+"F6.opExtrude","CAP_EDGE",EDGE,{"disambiguationData":[OSD([sQuery(id+"F5.wireOp",EDGE,"E2.sketch_text.stroke-115")])],"isStart":true})});
            var Q4;
            Q4=makeQuery(id+"F6.boolean.opBoolean","COPY",EDGE,{"derivedFrom":makeQuery(id+"F6.opExtrude","CAP_EDGE",EDGE,{"disambiguationData":[OSD([sQuery(id+"F5.wireOp",EDGE,"E2.sketch_text.stroke-119")])],"isStart":false})});
            var Q5;
            Q5=makeQuery(id+"F6.boolean.opBoolean","COPY",EDGE,{"derivedFrom":makeQuery(id+"F6.opExtrude","CAP_EDGE",EDGE,{"disambiguationData":[OSD([sQuery(id+"F5.wireOp",EDGE,"E2.sketch_text.stroke-111")])],"isStart":false})});
            var Q6;
            Q6=makeQuery(id+"F6.boolean.opBoolean","COPY",EDGE,{"derivedFrom":makeQuery(id+"F6.opExtrude","CAP_EDGE",EDGE,{"disambiguationData":[OSD([sQuery(id+"F5.wireOp",EDGE,"E2.sketch_text.stroke-122")])],"isStart":false})});
            var Q7;
            Q7=makeQuery(id+"F6.boolean.opBoolean","COPY",EDGE,{"derivedFrom":makeQuery(id+"F6.opExtrude","CAP_EDGE",EDGE,{"disambiguationData":[OSD([sQuery(id+"F5.wireOp",EDGE,"E2.sketch_text.stroke-115")])],"isStart":false})});
            fillet(context, id + "F12", {"entities" : qUnion([Q0, Q1, Q2, Q3, Q4, Q5, Q6, Q7]), "radius" : .2 * mm, "tangentPropagation" : true, "allowEdgeOverflow" : false});
        }
        {
            var Q0;
            Q0=makeQuery(id+"F6.boolean.opBoolean","COPY",EDGE,{"derivedFrom":makeQuery(id+"F6.opExtrude","CAP_EDGE",EDGE,{"disambiguationData":[OSD([sQuery(id+"F5.wireOp",EDGE,"E2.sketch_text.stroke-125")])],"isStart":true})});
            var Q1;
            Q1=makeQuery(id+"F6.boolean.opBoolean","COPY",EDGE,{"derivedFrom":makeQuery(id+"F6.opExtrude","CAP_EDGE",EDGE,{"disambiguationData":[OSD([sQuery(id+"F5.wireOp",EDGE,"E2.sketch_text.stroke-127")])],"isStart":true})});
            var Q2;
            Q2=makeQuery(id+"F6.boolean.opBoolean","COPY",EDGE,{"derivedFrom":makeQuery(id+"F6.opExtrude","CAP_EDGE",EDGE,{"disambiguationData":[OSD([sQuery(id+"F5.wireOp",EDGE,"E2.sketch_text.stroke-128")])],"isStart":true})});
            var Q3;
            Q3=makeQuery(id+"F6.boolean.opBoolean","COPY",EDGE,{"derivedFrom":makeQuery(id+"F6.opExtrude","CAP_EDGE",EDGE,{"disambiguationData":[OSD([sQuery(id+"F5.wireOp",EDGE,"E2.sketch_text.stroke-130")])],"isStart":true})});
            var Q4;
            Q4=makeQuery(id+"F6.boolean.opBoolean","COPY",EDGE,{"derivedFrom":makeQuery(id+"F6.opExtrude","CAP_EDGE",EDGE,{"disambiguationData":[OSD([sQuery(id+"F5.wireOp",EDGE,"E2.sketch_text.stroke-131")])],"isStart":true})});
            var Q5;
            Q5=makeQuery(id+"F6.boolean.opBoolean","COPY",EDGE,{"derivedFrom":makeQuery(id+"F6.opExtrude","CAP_EDGE",EDGE,{"disambiguationData":[OSD([sQuery(id+"F5.wireOp",EDGE,"E2.sketch_text.stroke-136")])],"isStart":true})});
            var Q6;
            Q6=makeQuery(id+"F6.boolean.opBoolean","COPY",EDGE,{"derivedFrom":makeQuery(id+"F6.opExtrude","CAP_EDGE",EDGE,{"disambiguationData":[OSD([sQuery(id+"F5.wireOp",EDGE,"E2.sketch_text.stroke-132")])],"isStart":true})});
            var Q7;
            Q7=makeQuery(id+"F6.boolean.opBoolean","COPY",EDGE,{"derivedFrom":makeQuery(id+"F6.opExtrude","CAP_EDGE",EDGE,{"disambiguationData":[OSD([sQuery(id+"F5.wireOp",EDGE,"E2.sketch_text.stroke-134")])],"isStart":true})});
            var Q8;
            Q8=makeQuery(id+"F6.boolean.opBoolean","COPY",EDGE,{"derivedFrom":makeQuery(id+"F6.opExtrude","CAP_EDGE",EDGE,{"disambiguationData":[OSD([sQuery(id+"F5.wireOp",EDGE,"E2.sketch_text.stroke-133")])],"isStart":true})});
            var Q9;
            Q9=makeQuery(id+"F6.boolean.opBoolean","COPY",EDGE,{"derivedFrom":makeQuery(id+"F6.opExtrude","CAP_EDGE",EDGE,{"disambiguationData":[OSD([sQuery(id+"F5.wireOp",EDGE,"E2.sketch_text.stroke-129")])],"isStart":true})});
            var Q10;
            Q10=makeQuery(id+"F6.boolean.opBoolean","COPY",EDGE,{"derivedFrom":makeQuery(id+"F6.opExtrude","CAP_EDGE",EDGE,{"disambiguationData":[OSD([sQuery(id+"F5.wireOp",EDGE,"E2.sketch_text.stroke-126")])],"isStart":true})});
            var Q11;
            Q11=makeQuery(id+"F6.boolean.opBoolean","COPY",EDGE,{"derivedFrom":makeQuery(id+"F6.opExtrude","CAP_EDGE",EDGE,{"disambiguationData":[OSD([sQuery(id+"F5.wireOp",EDGE,"E2.sketch_text.stroke-135")])],"isStart":true})});
            var Q12;
            Q12=makeQuery(id+"F6.boolean.opBoolean","COPY",EDGE,{"derivedFrom":makeQuery(id+"F6.opExtrude","CAP_EDGE",EDGE,{"disambiguationData":[OSD([sQuery(id+"F5.wireOp",EDGE,"E2.sketch_text.stroke-131")])],"isStart":false})});
            var Q13;
            Q13=makeQuery(id+"F6.boolean.opBoolean","COPY",EDGE,{"derivedFrom":makeQuery(id+"F6.opExtrude","CAP_EDGE",EDGE,{"disambiguationData":[OSD([sQuery(id+"F5.wireOp",EDGE,"E2.sketch_text.stroke-136")])],"isStart":false})});
            var Q14;
            Q14=makeQuery(id+"F6.boolean.opBoolean","COPY",EDGE,{"derivedFrom":makeQuery(id+"F6.opExtrude","CAP_EDGE",EDGE,{"disambiguationData":[OSD([sQuery(id+"F5.wireOp",EDGE,"E2.sketch_text.stroke-132")])],"isStart":false})});
            var Q15;
            Q15=makeQuery(id+"F6.boolean.opBoolean","COPY",EDGE,{"derivedFrom":makeQuery(id+"F6.opExtrude","CAP_EDGE",EDGE,{"disambiguationData":[OSD([sQuery(id+"F5.wireOp",EDGE,"E2.sketch_text.stroke-128")])],"isStart":false})});
            var Q16;
            Q16=makeQuery(id+"F6.boolean.opBoolean","COPY",EDGE,{"derivedFrom":makeQuery(id+"F6.opExtrude","CAP_EDGE",EDGE,{"disambiguationData":[OSD([sQuery(id+"F5.wireOp",EDGE,"E2.sketch_text.stroke-127")])],"isStart":false})});
            var Q17;
            Q17=makeQuery(id+"F6.boolean.opBoolean","COPY",EDGE,{"derivedFrom":makeQuery(id+"F6.opExtrude","CAP_EDGE",EDGE,{"disambiguationData":[OSD([sQuery(id+"F5.wireOp",EDGE,"E2.sketch_text.stroke-134")])],"isStart":false})});
            var Q18;
            Q18=makeQuery(id+"F6.boolean.opBoolean","COPY",EDGE,{"derivedFrom":makeQuery(id+"F6.opExtrude","CAP_EDGE",EDGE,{"disambiguationData":[OSD([sQuery(id+"F5.wireOp",EDGE,"E2.sketch_text.stroke-130")])],"isStart":false})});
            var Q19;
            Q19=makeQuery(id+"F6.boolean.opBoolean","COPY",EDGE,{"derivedFrom":makeQuery(id+"F6.opExtrude","CAP_EDGE",EDGE,{"disambiguationData":[OSD([sQuery(id+"F5.wireOp",EDGE,"E2.sketch_text.stroke-129")])],"isStart":false})});
            var Q20;
            Q20=makeQuery(id+"F6.boolean.opBoolean","COPY",EDGE,{"derivedFrom":makeQuery(id+"F6.opExtrude","CAP_EDGE",EDGE,{"disambiguationData":[OSD([sQuery(id+"F5.wireOp",EDGE,"E2.sketch_text.stroke-133")])],"isStart":false})});
            var Q21;
            Q21=makeQuery(id+"F6.boolean.opBoolean","COPY",EDGE,{"derivedFrom":makeQuery(id+"F6.opExtrude","CAP_EDGE",EDGE,{"disambiguationData":[OSD([sQuery(id+"F5.wireOp",EDGE,"E2.sketch_text.stroke-124")])],"isStart":false})});
            var Q22;
            Q22=makeQuery(id+"F6.boolean.opBoolean","COPY",EDGE,{"derivedFrom":makeQuery(id+"F6.opExtrude","CAP_EDGE",EDGE,{"disambiguationData":[OSD([sQuery(id+"F5.wireOp",EDGE,"E2.sketch_text.stroke-126")])],"isStart":false})});
            fillet(context, id + "F13", {"entities" : qUnion([Q0, Q1, Q2, Q3, Q4, Q5, Q6, Q7, Q8, Q9, Q10, Q11, Q12, Q13, Q14, Q15, Q16, Q17, Q18, Q19, Q20, Q21, Q22]), "radius" : .2 * mm, "tangentPropagation" : true, "allowEdgeOverflow" : false});
        }
        {
            var Q0;
            Q0=makeQuery(id+"F4.boolean.opBoolean","INTERSECT",EDGE,{"derivedFrom":[makeQuery(id+"F1.opExtrude","SWEPT_FACE",FACE,{"disambiguationData":[OSD([sQuery(id+"F0.wireOp",EDGE,"E0.bottom")])]}),makeQuery(id+"F4.opExtrude","SWEPT_FACE",FACE,{"disambiguationData":[OSD([sQuery(id+"F3.wireOp",EDGE,"E1")])]})]});
            fillet(context, id + "F14", {"entities" : qUnion([Q0]), "radius" : .2 * mm, "tangentPropagation" : true, "allowEdgeOverflow" : false});
        }
        {
            var Q0;
            Q0=makeQuery(id+"F4.boolean.opBoolean","INTERSECT",EDGE,{"derivedFrom":[makeQuery(id+"F1.opExtrude","SWEPT_FACE",FACE,{"disambiguationData":[OSD([sQuery(id+"F0.wireOp",EDGE,"E0.left")])]}),makeQuery(id+"F4.opExtrude","SWEPT_FACE",FACE,{"disambiguationData":[OSD([sQuery(id+"F3.wireOp",EDGE,"E1")])]})]});
            fillet(context, id + "F15", {"entities" : qUnion([Q0]), "radius" : .2 * mm, "tangentPropagation" : true, "allowEdgeOverflow" : false});
        }
    });
